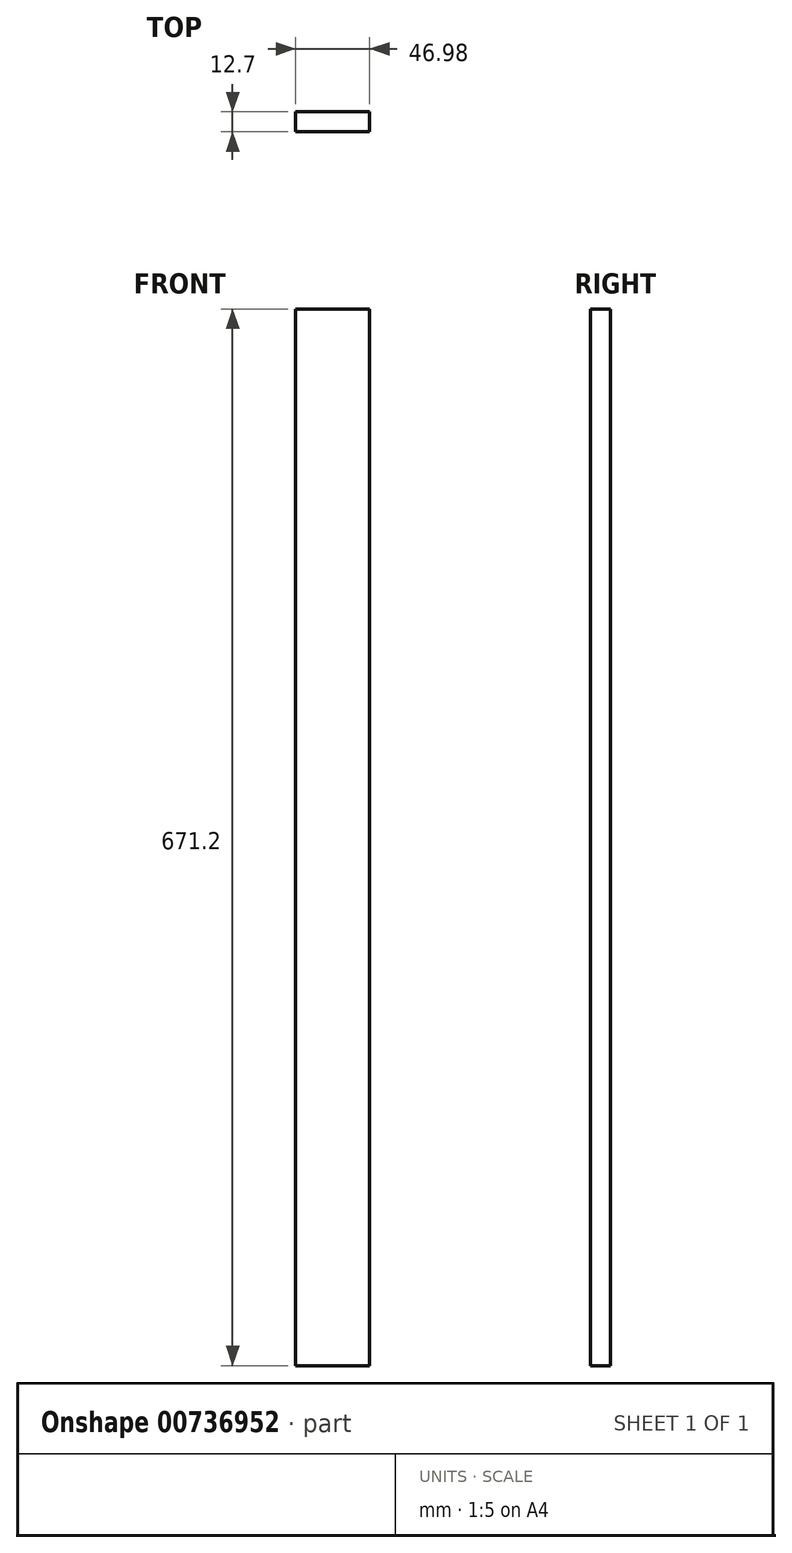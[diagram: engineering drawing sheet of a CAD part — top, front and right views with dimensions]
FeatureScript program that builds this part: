
annotation { "Feature Type Name" : "Feature", "Feature Type Description" : "" }
export const myFeature = defineFeature(function(context is Context, id is Id, definition is map)
    precondition{}
    {
        {
            var Q0;
            Q0=qCreatedBy(makeId("Front.planeOp"),FACE);
            var sketch = newSketch(context, id + "F0", { "sketchPlane" : qUnion([Q0])});
            skLineSegment(sketch, "E0.bottom", {"start": v(-23.5, 335.6) * mm, "end": v(23.5, 335.6) * mm});
            skLineSegment(sketch, "E0.top", {"start": v(-23.5, -335.6) * mm, "end": v(23.5, -335.6) * mm});
            skLineSegment(sketch, "E0.left", {"start": v(-23.5, 335.6) * mm, "end": v(-23.5, -335.6) * mm});
            skLineSegment(sketch, "E0.right", {"start": v(23.5, 335.6) * mm, "end": v(23.5, -335.6) * mm});
            skPoint(sketch, "E0.middle", {"position": v(0, 0) * mm});
            skSolve(sketch);
        }
        {
            var Q0;
            Q0 = qSketchRegion(id + "F0", true);
            extrude(context, id + "F1", {"entities" : qUnion([Q0]), "depth" : 12.7 * mm, "offsetDistance" : 25.4 * mm});
        }
    });
